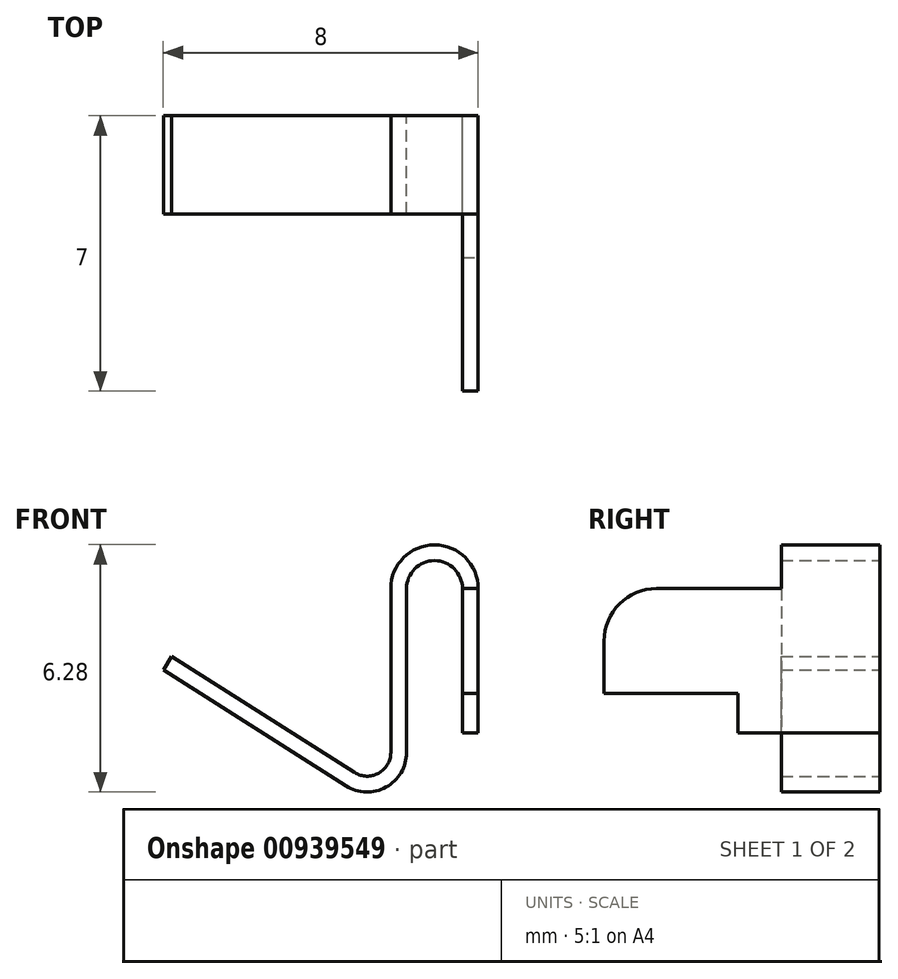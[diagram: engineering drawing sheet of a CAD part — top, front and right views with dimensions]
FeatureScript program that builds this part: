
annotation { "Feature Type Name" : "Feature", "Feature Type Description" : "" }
export const myFeature = defineFeature(function(context is Context, id is Id, definition is map)
    precondition{}
    {
        {
            var Q0;
            Q0=qCreatedBy(makeId("Front.planeOp"),FACE);
            var sketch = newSketch(context, id + "F0", { "sketchPlane" : qUnion([Q0])});
            skArc(sketch, "E0", {"start": v(0.71, 1.83) * mm, "mid": v(0, 2.55) * mm, "end": v(-0.71, 1.83) * mm, "construction": true});
            skArc(sketch, "E1", {"start": v(-0.71, -1.84) * mm, "mid": v(0, -2.55) * mm, "end": v(0.71, -1.84) * mm, "construction": true});
            skLineSegment(sketch, "E2", {"start": v(0.71, 1.83) * mm, "end": v(0.71, -1.84) * mm, "construction": true});
            skLineSegment(sketch, "E3", {"start": v(-0.71, 1.83) * mm, "end": v(-0.71, -1.84) * mm, "construction": true});
            skLineSegment(sketch, "E4", {"start": v(0.71, -1.84) * mm, "end": v(0.71, 1.84) * mm});
            skArc(sketch, "E5", {"start": v(0.71, 1.83) * mm, "mid": v(0, 2.55) * mm, "end": v(-0.71, 1.83) * mm});
            skLineSegment(sketch, "E6", {"start": v(-0.71, 1.83) * mm, "end": v(-0.71, -2.34) * mm});
            skArc(sketch, "E7", {"start": v(-0.71, -2.34) * mm, "mid": v(-1.23, -3.2) * mm, "end": v(-2.25, -3.18) * mm});
            skLineSegment(sketch, "E8", {"start": v(-2.25, -3.18) * mm, "end": v(-6.89, -0.23) * mm});
            skLineSegment(sketch, "E9.0", {"start": v(-2.03, -2.84) * mm, "end": v(-6.67, 0.11) * mm});
            skLineSegment(sketch, "E10.0", {"start": v(-1.1, 1.83) * mm, "end": v(-1.1, -2.33) * mm});
            skArc(sketch, "E11.0", {"start": v(1.1, 1.83) * mm, "mid": v(0, 2.94) * mm, "end": v(-1.11, 1.84) * mm});
            skLineSegment(sketch, "E12.0", {"start": v(1.1, -1.84) * mm, "end": v(1.1, 1.84) * mm});
            skLineSegment(sketch, "E13", {"start": v(0.71, -1.84) * mm, "end": v(1.1, -1.84) * mm});
            skLineSegment(sketch, "E14", {"start": v(-6.89, -0.23) * mm, "end": v(-6.67, 0.11) * mm});
            skArc(sketch, "E15", {"start": v(-1.1, -2.33) * mm, "mid": v(-1.42, -2.86) * mm, "end": v(-2.03, -2.84) * mm});
            skSolve(sketch);
        }
        {
            var Q0;
            Q0 = qSketchRegion(id + "F0", true);
            extrude(context, id + "F1", {"entities" : qUnion([Q0]), "depth" : 2.5 * mm, "offsetDistance" : 25 * mm});
        }
        {
            var Q0;
            Q0=makeQuery(id+"F1.opExtrude","CAP_FACE",FACE,{"disambiguationData":[OSD([sQuery(id+"F0.wireOp",EDGE,"E4"),sQuery(id+"F0.wireOp",EDGE,"E5"),sQuery(id+"F0.wireOp",EDGE,"E6"),sQuery(id+"F0.wireOp",EDGE,"E7"),sQuery(id+"F0.wireOp",EDGE,"E8"),sQuery(id+"F0.wireOp",EDGE,"E9.0"),sQuery(id+"F0.wireOp",EDGE,"E10.0"),sQuery(id+"F0.wireOp",EDGE,"E11.0"),sQuery(id+"F0.wireOp",EDGE,"E12.0"),sQuery(id+"F0.wireOp",EDGE,"E13"),sQuery(id+"F0.wireOp",EDGE,"E14"),sQuery(id+"F0.wireOp",EDGE,"E15")])],"isStart":false});
            var sketch = newSketch(context, id + "F2", { "sketchPlane" : qUnion([Q0])});
            skLineSegment(sketch, "E16.bottom", {"start": v(0.71, -1.84) * mm, "end": v(1.1, -1.84) * mm});
            skLineSegment(sketch, "E16.top", {"start": v(0.71, 1.84) * mm, "end": v(1.1, 1.84) * mm});
            skLineSegment(sketch, "E16.left", {"start": v(0.71, -1.84) * mm, "end": v(0.71, 1.84) * mm});
            skLineSegment(sketch, "E16.right", {"start": v(1.1, -1.84) * mm, "end": v(1.1, 1.84) * mm});
            skSolve(sketch);
        }
        {
            var Q0;
            Q0=makeQuery(id+"F2.imprint","IMPRINT",FACE,{"disambiguationData":[TD([[makeQuery(id+"F2.imprint","IMPRINT",EDGE,{"derivedFrom":sQuery(id+"F2.wireOp",EDGE,"E16.bottom")}),1.0]])]});
            extrude(context, id + "F3", {"entities" : qUnion([Q0]), "operationType" : NewBodyOperationType.ADD, "depth" : 4.5 * mm, "offsetDistance" : 25 * mm});
        }
        {
            var Q0;
            Q0=makeQuery(id+"F3.boolean.opBoolean","MERGE",FACE,{"derivedFrom":[makeQuery(id+"F1.opExtrude","SWEPT_FACE",FACE,{"disambiguationData":[OSD([sQuery(id+"F0.wireOp",EDGE,"E12.0")])]}),makeQuery(id+"F3.opExtrude","SWEPT_FACE",FACE,{"disambiguationData":[OSD([sQuery(id+"F2.wireOp",EDGE,"E16.right")])]})]});
            var sketch = newSketch(context, id + "F4", { "sketchPlane" : qUnion([Q0])});
            skLineSegment(sketch, "E17.bottom", {"start": v(-7, -1.84) * mm, "end": v(-3.6, -1.84) * mm});
            skLineSegment(sketch, "E17.top", {"start": v(-7, -0.84) * mm, "end": v(-3.6, -0.84) * mm});
            skLineSegment(sketch, "E17.left", {"start": v(-7, -1.84) * mm, "end": v(-7, -0.84) * mm});
            skLineSegment(sketch, "E17.right", {"start": v(-3.6, -1.84) * mm, "end": v(-3.6, -0.83) * mm});
            skSolve(sketch);
        }
        {
            var Q0;
            Q0 = qSketchRegion(id + "F4", true);
            extrude(context, id + "F5", {"entities" : qUnion([Q0]), "operationType" : NewBodyOperationType.REMOVE, "oppositeDirection" : true, "depth" : 25 * mm, "offsetDistance" : 25 * mm});
        }
        {
            var Q0;
            Q0=makeQuery(id+"F3.opExtrude","CAP_EDGE",EDGE,{"disambiguationData":[OSD([sQuery(id+"F2.wireOp",EDGE,"E16.top")])],"isStart":false});
            var Q1;
            Q1=makeQuery(id+"F5.boolean.opBoolean","COPY",EDGE,{"derivedFrom":makeQuery(id+"F5.opExtrude","SWEPT_EDGE",EDGE,{"disambiguationData":[OSD([sQuery(id+"F2.wireOp",EDGE,"E16.right"),sQuery(id+"F4.wireOp",EDGE,"E17.top"),sQuery(id+"F4.wireOp",EDGE,"E17.left")])]})});
            fillet(context, id + "F6", {"entities" : qUnion([Q0, Q1]), "radius" : 1.33 * mm, "tangentPropagation" : true, "allowEdgeOverflow" : false});
        }
    });
